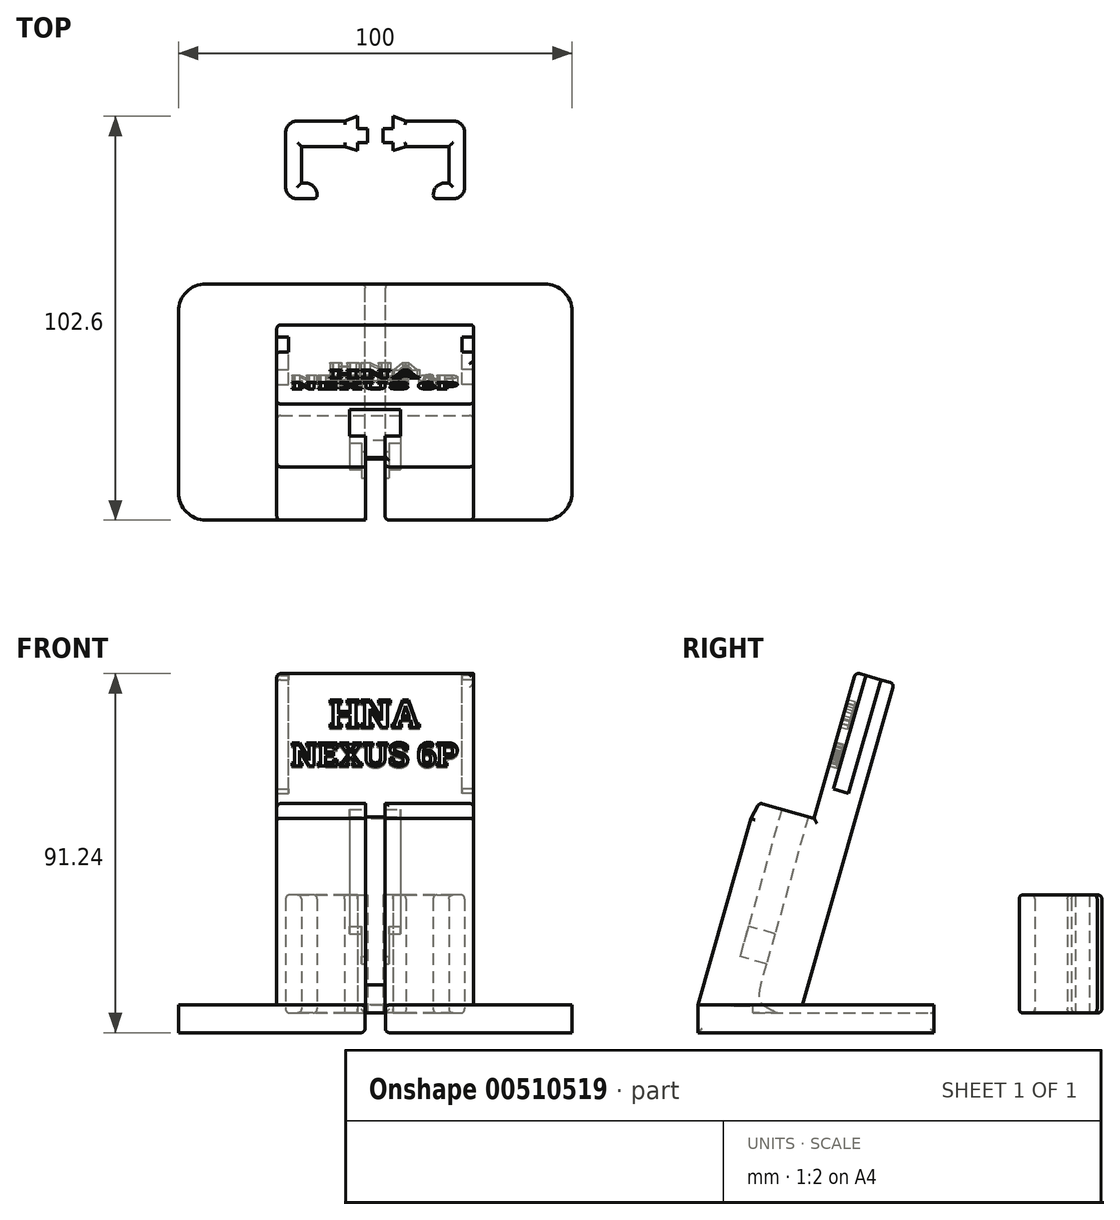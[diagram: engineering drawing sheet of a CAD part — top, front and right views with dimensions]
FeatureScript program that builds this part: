
annotation { "Feature Type Name" : "Feature", "Feature Type Description" : "" }
export const myFeature = defineFeature(function(context is Context, id is Id, definition is map)
    precondition{}
    {
        {
            var Q0;
            Q0=qCreatedBy(makeId("Top.planeOp"),FACE);
            var sketch = newSketch(context, id + "F0", { "sketchPlane" : qUnion([Q0])});
            skLineSegment(sketch, "E0.bottom", {"start": v(50, -30) * mm, "end": v(-50, -30) * mm});
            skLineSegment(sketch, "E0.top", {"start": v(50, 30) * mm, "end": v(-50, 30) * mm});
            skLineSegment(sketch, "E0.left", {"start": v(50, -30) * mm, "end": v(50, 30) * mm});
            skLineSegment(sketch, "E0.right", {"start": v(-50, -30) * mm, "end": v(-50, 30) * mm});
            skPoint(sketch, "E0.middle", {"position": v(0, 0) * mm});
            skLineSegment(sketch, "E1.top", {"start": v(25, -4) * mm, "end": v(-25, -4) * mm});
            skLineSegment(sketch, "E1.left", {"start": v(25, -30) * mm, "end": v(25, -4) * mm});
            skLineSegment(sketch, "E1.right", {"start": v(-25, -30) * mm, "end": v(-25, -4) * mm});
            skPoint(sketch, "E1.middle", {"position": v(0, -17) * mm});
            skLineSegment(sketch, "E2", {"start": v(0, -28.9) * mm, "end": v(-2.6, -28.9) * mm, "construction": true});
            skLineSegment(sketch, "E3", {"start": v(-2.6, -30) * mm, "end": v(-2.6, 30) * mm});
            skLineSegment(sketch, "E4", {"start": v(0, -28.9) * mm, "end": v(2.6, -28.9) * mm});
            skLineSegment(sketch, "E5", {"start": v(2.6, -30) * mm, "end": v(2.6, 30) * mm});
            skLineSegment(sketch, "E6", {"start": v(2.6, -16) * mm, "end": v(-2.6, -16) * mm});
            skLineSegment(sketch, "E7", {"start": v(-2.5, 71.41) * mm, "end": v(-20.75, 71.41) * mm});
            skLineSegment(sketch, "E8", {"start": v(-20.75, 71.41) * mm, "end": v(-20.75, 51.61) * mm});
            skLineSegment(sketch, "E9", {"start": v(-20.75, 51.61) * mm, "end": v(-12.75, 51.61) * mm});
            skLineSegment(sketch, "E10", {"start": v(-12.75, 51.61) * mm, "end": v(-12.75, 55.61) * mm});
            skLineSegment(sketch, "E11", {"start": v(-12.75, 55.61) * mm, "end": v(-16.75, 55.61) * mm});
            skLineSegment(sketch, "E12", {"start": v(-16.75, 55.61) * mm, "end": v(-16.75, 64.91) * mm});
            skLineSegment(sketch, "E13", {"start": v(-16.75, 64.91) * mm, "end": v(-2.5, 64.91) * mm});
            skLineSegment(sketch, "E14", {"start": v(0, 65.91) * mm, "end": v(0, 69.41) * mm});
            skLineSegment(sketch, "E15", {"start": v(-2.5, 64.91) * mm, "end": v(-2.5, 65.91) * mm});
            skLineSegment(sketch, "E16", {"start": v(-2.5, 65.91) * mm, "end": v(0, 65.91) * mm});
            skLineSegment(sketch, "E17", {"start": v(-2.5, 71.41) * mm, "end": v(-2.5, 69.41) * mm});
            skLineSegment(sketch, "E18", {"start": v(-2.5, 69.41) * mm, "end": v(0, 69.41) * mm});
            skLineSegment(sketch, "E19", {"start": v(-5.78, 71.41) * mm, "end": v(-2.5, 72.6) * mm});
            skLineSegment(sketch, "E20", {"start": v(-2.5, 72.6) * mm, "end": v(-2.5, 71.41) * mm});
            skLineSegment(sketch, "E21", {"start": v(-2.5, 64.91) * mm, "end": v(-2.5, 63.9) * mm});
            skLineSegment(sketch, "E22", {"start": v(-2.5, 63.9) * mm, "end": v(-5.78, 64.91) * mm});
            skSolve(sketch);
        }
        {
            var Q0;
            {var subQ4=sQuery(id+"F0.wireOp",EDGE,"E0.right");Q0=makeQuery(id+"F0.imprint","IMPRINT",FACE,{"disambiguationData":[TD([[makeQuery(id+"F0.imprint","IMPRINT",EDGE,{"derivedFrom":subQ4}),-1.0]])]});}
            var Q1;
            {var subQ0=sQuery(id+"F0.wireOp",EDGE,"E1.right");Q1=makeQuery(id+"F0.imprint","IMPRINT",FACE,{"disambiguationData":[TD([[makeQuery(id+"F0.imprint","IMPRINT",EDGE,{"derivedFrom":subQ0}),-1.0]])]});}
            var Q2;
            {var subQ4=sQuery(id+"F0.wireOp",EDGE,"E1.left");Q2=makeQuery(id+"F0.imprint","IMPRINT",FACE,{"disambiguationData":[TD([[makeQuery(id+"F0.imprint","IMPRINT",EDGE,{"derivedFrom":subQ4}),1.0]])]});}
            var Q3;
            {var subQ0=sQuery(id+"F0.wireOp",EDGE,"E0.left");Q3=makeQuery(id+"F0.imprint","IMPRINT",FACE,{"disambiguationData":[TD([[makeQuery(id+"F0.imprint","IMPRINT",EDGE,{"derivedFrom":subQ0}),1.0]])]});}
            extrude(context, id + "F1", {"entities" : qUnion([Q0, Q1, Q2, Q3]), "oppositeDirection" : true, "depth" : 5 * mm});
        }
        {
            var Q0;
            {var subQ4=sQuery(id+"F0.wireOp",EDGE,"E0.right");Q0=makeQuery(id+"F0.imprint","IMPRINT",FACE,{"disambiguationData":[TD([[makeQuery(id+"F0.imprint","IMPRINT",EDGE,{"derivedFrom":subQ4}),-1.0]])]});}
            var Q1;
            {var subQ0=sQuery(id+"F0.wireOp",EDGE,"E1.right");Q1=makeQuery(id+"F0.imprint","IMPRINT",FACE,{"disambiguationData":[TD([[makeQuery(id+"F0.imprint","IMPRINT",EDGE,{"derivedFrom":subQ0}),-1.0]])]});}
            var Q2;
            {var subQ0=sQuery(id+"F0.wireOp",EDGE,"E3");var subQ1=sQuery(id+"F0.wireOp",EDGE,"E0.top");var subQ2=makeQuery(id+"F0.imprint","INTERSECT",VERTEX,{"derivedFrom":[subQ1,subQ0]});Q2=makeQuery(id+"F0.imprint","IMPRINT",FACE,{"disambiguationData":[TD([[makeQuery(id+"F0.imprint","IMPRINT",EDGE,{"disambiguationData":[TD([[subQ2,1.0]])],"derivedFrom":subQ1}),1.0]])]});}
            var Q3;
            {var subQ4=sQuery(id+"F0.wireOp",EDGE,"E1.left");Q3=makeQuery(id+"F0.imprint","IMPRINT",FACE,{"disambiguationData":[TD([[makeQuery(id+"F0.imprint","IMPRINT",EDGE,{"derivedFrom":subQ4}),1.0]])]});}
            var Q4;
            {var subQ0=sQuery(id+"F0.wireOp",EDGE,"E0.left");Q4=makeQuery(id+"F0.imprint","IMPRINT",FACE,{"disambiguationData":[TD([[makeQuery(id+"F0.imprint","IMPRINT",EDGE,{"derivedFrom":subQ0}),1.0]])]});}
            var Q5;
            {var subQ5=sQuery(id+"F0.wireOp",EDGE,"E6");Q5=makeQuery(id+"F0.imprint","IMPRINT",FACE,{"disambiguationData":[TD([[makeQuery(id+"F0.imprint","IMPRINT",EDGE,{"derivedFrom":subQ5}),-1.0]])]});}
            extrude(context, id + "F2", {"entities" : qUnion([Q0, Q1, Q2, Q3, Q4, Q5]), "operationType" : NewBodyOperationType.ADD, "depth" : 2 * mm});
        }
        {
            var Q0;
            Q0=makeQuery(id+"F2.opExtrude","CAP_FACE",FACE,{"disambiguationData":[OSD([sQuery(id+"F0.wireOp",EDGE,"E0.bottom"),sQuery(id+"F0.wireOp",EDGE,"E0.top"),sQuery(id+"F0.wireOp",EDGE,"E0.left"),sQuery(id+"F0.wireOp",EDGE,"E0.right"),sQuery(id+"F0.wireOp",EDGE,"E1.top"),sQuery(id+"F0.wireOp",EDGE,"E3"),sQuery(id+"F0.wireOp",EDGE,"E5")])],"isStart":false});
            var sketch = newSketch(context, id + "F3", { "sketchPlane" : qUnion([Q0])});
            skLineSegment(sketch, "E23.bottom", {"start": v(50, -30) * mm, "end": v(-50, -30) * mm});
            skLineSegment(sketch, "E23.top", {"start": v(50, 30) * mm, "end": v(-50, 30) * mm});
            skLineSegment(sketch, "E23.left", {"start": v(50, -30) * mm, "end": v(50, 30) * mm});
            skLineSegment(sketch, "E23.right", {"start": v(-50, -30) * mm, "end": v(-50, 30) * mm});
            skPoint(sketch, "E23.middle", {"position": v(0, 0) * mm});
            skLineSegment(sketch, "E24.top", {"start": v(25, -4) * mm, "end": v(-25, -4) * mm});
            skLineSegment(sketch, "E24.left", {"start": v(25, -30) * mm, "end": v(25, -4) * mm});
            skLineSegment(sketch, "E24.right", {"start": v(-25, -30) * mm, "end": v(-25, -4) * mm});
            skPoint(sketch, "E24.middle", {"position": v(0, -17) * mm});
            skLineSegment(sketch, "E25", {"start": v(0, -20.22) * mm, "end": v(-2.6, -20.22) * mm, "construction": true});
            skLineSegment(sketch, "E26", {"start": v(0, -20.22) * mm, "end": v(2.6, -20.22) * mm});
            skLineSegment(sketch, "E27", {"start": v(-2.6, -16) * mm, "end": v(2.6, -16) * mm});
            skSolve(sketch);
        }
        {
            var Q0;
            Q0=qCreatedBy(makeId("Right.planeOp"),FACE);
            var sketch = newSketch(context, id + "F4", { "sketchPlane" : qUnion([Q0])});
            skLineSegment(sketch, "E28", {"start": v(-30, 2) * mm, "end": v(-16.48, 49.44) * mm});
            skLineSegment(sketch, "E29", {"start": v(-16.48, 49.44) * mm, "end": v(10.06, 49.44) * mm});
            skLineSegment(sketch, "E30", {"start": v(10.06, 49.44) * mm, "end": v(-3.6, 1.55) * mm});
            skLineSegment(sketch, "E31", {"start": v(-3.6, 1.55) * mm, "end": v(-30, 2) * mm});
            skLineSegment(sketch, "E32", {"start": v(10.06, 49.44) * mm, "end": v(20.62, 86.48) * mm});
            skLineSegment(sketch, "E33", {"start": v(20.62, 86.48) * mm, "end": v(10.06, 86.48) * mm});
            skLineSegment(sketch, "E34", {"start": v(10.06, 86.48) * mm, "end": v(-0.5, 49.44) * mm});
            skLineSegment(sketch, "E35", {"start": v(-0.5, 49.44) * mm, "end": v(-1.94, 49.85) * mm});
            skLineSegment(sketch, "E36", {"start": v(-1.94, 49.85) * mm, "end": v(-10.41, 20.13) * mm});
            skLineSegment(sketch, "E37.0", {"start": v(-8.67, 51.77) * mm, "end": v(-17.14, 22.05) * mm});
            skLineSegment(sketch, "E38", {"start": v(-10.41, 20.13) * mm, "end": v(-17.14, 22.05) * mm});
            skLineSegment(sketch, "E39", {"start": v(-8.67, 51.77) * mm, "end": v(-14.37, 53.39) * mm});
            skLineSegment(sketch, "E40", {"start": v(-14.37, 53.39) * mm, "end": v(-16.48, 49.44) * mm});
            skLineSegment(sketch, "E41", {"start": v(-10.41, 20.13) * mm, "end": v(-12.6, 12.44) * mm});
            skLineSegment(sketch, "E42.0", {"start": v(-17.14, 22.05) * mm, "end": v(-19.34, 14.36) * mm});
            skLineSegment(sketch, "E43", {"start": v(-12.6, 12.44) * mm, "end": v(-19.34, 14.36) * mm});
            skLineSegment(sketch, "E44", {"start": v(-12.6, 12.44) * mm, "end": v(-15.65, 1.75) * mm});
            skLineSegment(sketch, "E45", {"start": v(-19.34, 14.36) * mm, "end": v(-22.9, 1.88) * mm});
            skPoint(sketch, "E46.1.internal.snap0", {"position": v(-14.13, 7.1) * mm});
            skFitSpline(sketch, "E46", {"points": [v(-14.13, 7.1) * mm, v(-14.13, 2.85) * mm, v(-9.8, 0) * mm], "startDerivative": vector(-1.86, -9.65) * mm, "endDerivative": vector(10, -5.58) * mm});
            skLineSegment(sketch, "E47", {"start": v(-9.8, 0) * mm, "end": v(-30.07, 0) * mm});
            skLineSegment(sketch, "E48", {"start": v(-30.07, 0) * mm, "end": v(-30, 2) * mm});
            skLineSegment(sketch, "E49", {"start": v(-1.94, 49.85) * mm, "end": v(-8.67, 51.77) * mm});
            skLineSegment(sketch, "E50", {"start": v(10.06, 86.48) * mm, "end": v(19.83, 83.7) * mm});
            skSolve(sketch);
        }
        {
            var Q0;
            {var subQ3=sQuery(id+"F4.wireOp",EDGE,"E28");Q0=makeQuery(id+"F4.imprint","IMPRINT",FACE,{"disambiguationData":[TD([[makeQuery(id+"F4.imprint","IMPRINT",EDGE,{"derivedFrom":subQ3}),-1.0]])]});}
            var Q1;
            Q1=makeQuery(id+"F4.imprint","IMPRINT",FACE,{"disambiguationData":[TD([[makeQuery(id+"F4.imprint","IMPRINT",EDGE,{"derivedFrom":sQuery(id+"F4.wireOp",EDGE,"E43")}),1.0]])]});
            var Q2;
            {var subQ4=sQuery(id+"F4.wireOp",EDGE,"E41");Q2=makeQuery(id+"F4.imprint","IMPRINT",FACE,{"disambiguationData":[TD([[makeQuery(id+"F4.imprint","IMPRINT",EDGE,{"derivedFrom":subQ4}),-1.0]])]});}
            var Q3;
            {var subQ1=sQuery(id+"F4.wireOp",EDGE,"E30");Q3=makeQuery(id+"F4.imprint","IMPRINT",FACE,{"disambiguationData":[TD([[makeQuery(id+"F4.imprint","IMPRINT",EDGE,{"derivedFrom":subQ1}),-1.0]])]});}
            var Q4;
            {var subQ4=sQuery(id+"F4.wireOp",EDGE,"E39");Q4=makeQuery(id+"F4.imprint","IMPRINT",FACE,{"disambiguationData":[TD([[makeQuery(id+"F4.imprint","IMPRINT",EDGE,{"derivedFrom":subQ4}),1.0]])]});}
            var Q5;
            {var subQ0=sQuery(id+"F4.wireOp",EDGE,"E35");Q5=makeQuery(id+"F4.imprint","IMPRINT",FACE,{"disambiguationData":[TD([[makeQuery(id+"F4.imprint","IMPRINT",EDGE,{"derivedFrom":subQ0}),1.0]])]});}
            var Q6;
            {var subQ0=sQuery(id+"F4.wireOp",EDGE,"E44");var subQ1=sQuery(id+"F4.wireOp",EDGE,"E31");var subQ2=makeQuery(id+"F4.imprint","INTERSECT",VERTEX,{"derivedFrom":[subQ1,subQ0]});Q6=makeQuery(id+"F4.imprint","IMPRINT",FACE,{"disambiguationData":[TD([[makeQuery(id+"F4.imprint","IMPRINT",EDGE,{"disambiguationData":[TD([[subQ2,1.0]])],"derivedFrom":subQ1}),-1.0]])]});}
            var Q7;
            {var subQ5=sQuery(id+"F4.wireOp",EDGE,"E49");Q7=makeQuery(id+"F4.imprint","IMPRINT",FACE,{"disambiguationData":[TD([[makeQuery(id+"F4.imprint","IMPRINT",EDGE,{"derivedFrom":subQ5}),1.0]])]});}
            var Q8;
            {var subQ3=sQuery(id+"F4.wireOp",EDGE,"E34");Q8=makeQuery(id+"F4.imprint","IMPRINT",FACE,{"disambiguationData":[TD([[makeQuery(id+"F4.imprint","IMPRINT",EDGE,{"derivedFrom":subQ3}),1.0]])]});}
            var Q9;
            {var subQ5=sQuery(id+"F4.wireOp",EDGE,"E38");Q9=makeQuery(id+"F4.imprint","IMPRINT",FACE,{"disambiguationData":[TD([[makeQuery(id+"F4.imprint","IMPRINT",EDGE,{"derivedFrom":subQ5}),-1.0]])]});}
            extrude(context, id + "F5", {"entities" : qUnion([Q0, Q1, Q2, Q3, Q4, Q5, Q6, Q7, Q8, Q9]), "operationType" : NewBodyOperationType.ADD, "endBound" : BoundingType.SYMMETRIC, "oppositeDirection" : true, "depth" : 50 * mm});
        }
        {
            var Q0;
            {var subQ5=sQuery(id+"F4.wireOp",EDGE,"E49");Q0=makeQuery(id+"F4.imprint","IMPRINT",FACE,{"disambiguationData":[TD([[makeQuery(id+"F4.imprint","IMPRINT",EDGE,{"derivedFrom":subQ5}),1.0]])]});}
            var Q1;
            {var subQ5=sQuery(id+"F4.wireOp",EDGE,"E38");Q1=makeQuery(id+"F4.imprint","IMPRINT",FACE,{"disambiguationData":[TD([[makeQuery(id+"F4.imprint","IMPRINT",EDGE,{"derivedFrom":subQ5}),-1.0]])]});}
            extrude(context, id + "F6", {"entities" : qUnion([Q0, Q1]), "operationType" : NewBodyOperationType.REMOVE, "endBound" : BoundingType.SYMMETRIC, "oppositeDirection" : true, "depth" : 13 * mm});
        }
        {
            var Q0;
            {var subQ4=sQuery(id+"F4.wireOp",EDGE,"E47");Q0=makeQuery(id+"F4.imprint","IMPRINT",FACE,{"disambiguationData":[TD([[makeQuery(id+"F4.imprint","IMPRINT",EDGE,{"derivedFrom":subQ4}),-1.0]])]});}
            var Q1;
            {var subQ0=sQuery(id+"F4.wireOp",EDGE,"E44");var subQ1=sQuery(id+"F4.wireOp",EDGE,"E31");var subQ2=makeQuery(id+"F4.imprint","INTERSECT",VERTEX,{"derivedFrom":[subQ1,subQ0]});Q1=makeQuery(id+"F4.imprint","IMPRINT",FACE,{"disambiguationData":[TD([[makeQuery(id+"F4.imprint","IMPRINT",EDGE,{"disambiguationData":[TD([[subQ2,1.0]])],"derivedFrom":subQ1}),-1.0]])]});}
            var Q2;
            {var subQ4=sQuery(id+"F4.wireOp",EDGE,"E43");Q2=makeQuery(id+"F4.imprint","IMPRINT",FACE,{"disambiguationData":[TD([[makeQuery(id+"F4.imprint","IMPRINT",EDGE,{"derivedFrom":subQ4}),1.0]])]});}
            var Q3;
            {var subQ5=sQuery(id+"F4.wireOp",EDGE,"E28");Q3=makeQuery(id+"F4.imprint","IMPRINT",FACE,{"disambiguationData":[TD([[makeQuery(id+"F4.imprint","IMPRINT",EDGE,{"derivedFrom":subQ5}),-1.0]])]});}
            var Q4;
            {var subQ4=sQuery(id+"F4.wireOp",EDGE,"E39");Q4=makeQuery(id+"F4.imprint","IMPRINT",FACE,{"disambiguationData":[TD([[makeQuery(id+"F4.imprint","IMPRINT",EDGE,{"derivedFrom":subQ4}),1.0]])]});}
            extrude(context, id + "F7", {"entities" : qUnion([Q0, Q1, Q2, Q3, Q4]), "operationType" : NewBodyOperationType.REMOVE, "endBound" : BoundingType.SYMMETRIC, "depth" : 5 * mm});
        }
        {
            var Q0;
            Q0=makeQuery(id+"F4.imprint","IMPRINT",FACE,{"disambiguationData":[TD([[makeQuery(id+"F4.imprint","IMPRINT",EDGE,{"derivedFrom":sQuery(id+"F4.wireOp",EDGE,"E38")}),1.0]])]});
            extrude(context, id + "F8", {"entities" : qUnion([Q0]), "operationType" : NewBodyOperationType.REMOVE, "endBound" : BoundingType.SYMMETRIC, "oppositeDirection" : true, "depth" : 7 * mm});
        }
        {
            var Q0;
            Q0=makeQuery(id+"F5.opExtrude","SWEPT_FACE",FACE,{"disambiguationData":[OSD([sQuery(id+"F4.wireOp",EDGE,"E50")])]});
            var sketch = newSketch(context, id + "F9", { "sketchPlane" : qUnion([Q0])});
            skLineSegment(sketch, "E51.bottom", {"start": v(-25, -11.33) * mm, "end": v(-22, -11.33) * mm});
            skLineSegment(sketch, "E51.top", {"start": v(-25, -7.33) * mm, "end": v(-22, -7.33) * mm});
            skLineSegment(sketch, "E51.left", {"start": v(-25, -11.33) * mm, "end": v(-25, -7.33) * mm});
            skLineSegment(sketch, "E51.right", {"start": v(-22, -11.33) * mm, "end": v(-22, -7.33) * mm});
            skLineSegment(sketch, "E52.MirrorCS", {"start": v(22, -11.33) * mm, "end": v(22, -7.33) * mm});
            skLineSegment(sketch, "E53.MirrorCS", {"start": v(25, -7.33) * mm, "end": v(22, -7.33) * mm});
            skLineSegment(sketch, "E54.MirrorCS", {"start": v(25, -11.33) * mm, "end": v(22, -11.33) * mm});
            skLineSegment(sketch, "E55.MirrorCS", {"start": v(25, -11.33) * mm, "end": v(25, -7.33) * mm});
            skSolve(sketch);
        }
        {
            var Q0;
            Q0=makeQuery(id+"F9.imprint","IMPRINT",FACE,{"disambiguationData":[TD([[makeQuery(id+"F9.imprint","IMPRINT",EDGE,{"derivedFrom":sQuery(id+"F9.wireOp",EDGE,"E52.MirrorCS")}),-1.0]])]});
            var Q1;
            Q1=makeQuery(id+"F9.imprint","IMPRINT",FACE,{"disambiguationData":[TD([[makeQuery(id+"F9.imprint","IMPRINT",EDGE,{"derivedFrom":sQuery(id+"F9.wireOp",EDGE,"E51.bottom")}),1.0]])]});
            extrude(context, id + "F10", {"entities" : qUnion([Q0, Q1]), "operationType" : NewBodyOperationType.REMOVE, "oppositeDirection" : true, "depth" : 30 * mm});
        }
        {
            var Q0;
            Q0=makeQuery(id+"F5.opExtrude","SWEPT_FACE",FACE,{"disambiguationData":[OSD([sQuery(id+"F4.wireOp",EDGE,"E34")])]});
            var sketch = newSketch(context, id + "F11", { "sketchPlane" : qUnion([Q0])});
            skText(sketch, "E56", { "text": "HNA", "fontName": "RobotoSlab-Bold.ttf"});
            skText(sketch, "E57", { "text": "NEXUS 6P", "fontName": "RobotoSlab-Bold.ttf"});
            const initialGuessF11  = {"E56": [-0.0118, 0.07148, 1, 0, 0.00735], "E57": [-0.02139, 0.06127, 1, 0, 0.0062]};
            skSetInitialGuess(sketch, initialGuessF11);
            skSolve(sketch);
        }
        {
            var Q0;
            Q0=makeQuery(id+"F11.imprint","IMPRINT",FACE,{"disambiguationData":[TD([[makeQuery(id+"F11.imprint","IMPRINT",EDGE,{"derivedFrom":sQuery(id+"F11.wireOp",EDGE,"E56.sketch_text.stroke-54")}),-1.0]])]});
            var Q1;
            Q1=makeQuery(id+"F11.imprint","IMPRINT",FACE,{"disambiguationData":[TD([[makeQuery(id+"F11.imprint","IMPRINT",EDGE,{"derivedFrom":sQuery(id+"F11.wireOp",EDGE,"E56.sketch_text.stroke-30")}),-1.0]])]});
            var Q2;
            Q2=makeQuery(id+"F11.imprint","IMPRINT",FACE,{"disambiguationData":[TD([[makeQuery(id+"F11.imprint","IMPRINT",EDGE,{"derivedFrom":sQuery(id+"F11.wireOp",EDGE,"E56.sketch_text.stroke-0")}),-1.0]])]});
            var Q3;
            Q3=makeQuery(id+"F11.imprint","IMPRINT",FACE,{"disambiguationData":[TD([[makeQuery(id+"F11.imprint","IMPRINT",EDGE,{"derivedFrom":sQuery(id+"F11.wireOp",EDGE,"E57.sketch_text.stroke-155")}),-1.0]])]});
            var Q4;
            Q4=makeQuery(id+"F11.imprint","IMPRINT",FACE,{"disambiguationData":[TD([[makeQuery(id+"F11.imprint","IMPRINT",EDGE,{"derivedFrom":sQuery(id+"F11.wireOp",EDGE,"E57.sketch_text.stroke-127")}),-1.0]])]});
            var Q5;
            Q5=makeQuery(id+"F11.imprint","IMPRINT",FACE,{"disambiguationData":[TD([[makeQuery(id+"F11.imprint","IMPRINT",EDGE,{"derivedFrom":sQuery(id+"F11.wireOp",EDGE,"E57.sketch_text.stroke-97")}),-1.0]])]});
            var Q6;
            Q6=makeQuery(id+"F11.imprint","IMPRINT",FACE,{"disambiguationData":[TD([[makeQuery(id+"F11.imprint","IMPRINT",EDGE,{"derivedFrom":sQuery(id+"F11.wireOp",EDGE,"E57.sketch_text.stroke-73")}),-1.0]])]});
            var Q7;
            Q7=makeQuery(id+"F11.imprint","IMPRINT",FACE,{"disambiguationData":[TD([[makeQuery(id+"F11.imprint","IMPRINT",EDGE,{"derivedFrom":sQuery(id+"F11.wireOp",EDGE,"E57.sketch_text.stroke-45")}),-1.0]])]});
            var Q8;
            Q8=makeQuery(id+"F11.imprint","IMPRINT",FACE,{"disambiguationData":[TD([[makeQuery(id+"F11.imprint","IMPRINT",EDGE,{"derivedFrom":sQuery(id+"F11.wireOp",EDGE,"E57.sketch_text.stroke-24")}),-1.0]])]});
            var Q9;
            Q9=makeQuery(id+"F11.imprint","IMPRINT",FACE,{"disambiguationData":[TD([[makeQuery(id+"F11.imprint","IMPRINT",EDGE,{"derivedFrom":sQuery(id+"F11.wireOp",EDGE,"E57.sketch_text.stroke-0")}),-1.0]])]});
            extrude(context, id + "F12", {"entities" : qUnion([Q0, Q1, Q2, Q3, Q4, Q5, Q6, Q7, Q8, Q9]), "operationType" : NewBodyOperationType.REMOVE, "oppositeDirection" : true, "depth" : 2 * mm});
        }
        {
            var Q0;
            {var subQ0=sQuery(id+"F4.wireOp",EDGE,"E50");var subQ1=sQuery(id+"F4.wireOp",EDGE,"E34");Q0=makeQuery(id+"F10.boolean.opBoolean","SPLIT",EDGE,{"disambiguationData":[TD([makeQuery(id+"F5.opExtrude","SWEPT_FACE",FACE,{"disambiguationData":[OSD([subQ1])]})])],"derivedFrom":makeQuery(id+"F5.opExtrude","CAP_EDGE",EDGE,{"disambiguationData":[OSD([subQ0])],"isStart":false})});}
            var Q1;
            {var subQ0=sQuery(id+"F4.wireOp",EDGE,"E50");Q1=makeQuery(id+"F10.boolean.opBoolean","SPLIT",EDGE,{"disambiguationData":[TD([makeQuery(id+"F10.opExtrude","SWEPT_FACE",FACE,{"disambiguationData":[OSD([sQuery(id+"F9.wireOp",EDGE,"E51.top")])]})])],"derivedFrom":makeQuery(id+"F5.opExtrude","CAP_EDGE",EDGE,{"disambiguationData":[OSD([subQ0])],"isStart":false})});}
            var Q2;
            Q2=makeQuery(id+"F10.boolean.opBoolean","COPY",EDGE,{"derivedFrom":makeQuery(id+"F10.opExtrude","SWEPT_EDGE",EDGE,{"disambiguationData":[OSD([sQuery(id+"F4.wireOp",EDGE,"E50"),sQuery(id+"F9.wireOp",EDGE,"E51.top"),sQuery(id+"F9.wireOp",EDGE,"E51.left")])]})});
            var Q3;
            Q3=makeQuery(id+"F10.boolean.opBoolean","COPY",EDGE,{"derivedFrom":makeQuery(id+"F10.opExtrude","SWEPT_EDGE",EDGE,{"disambiguationData":[OSD([sQuery(id+"F4.wireOp",EDGE,"E50"),sQuery(id+"F9.wireOp",EDGE,"E51.bottom"),sQuery(id+"F9.wireOp",EDGE,"E51.left")])]})});
            var Q4;
            Q4=makeQuery(id+"F10.boolean.opBoolean","COPY",EDGE,{"derivedFrom":makeQuery(id+"F10.opExtrude","CAP_EDGE",EDGE,{"disambiguationData":[OSD([sQuery(id+"F9.wireOp",EDGE,"E51.left")])],"isStart":false})});
            var Q5;
            Q5=makeQuery(id+"F10.boolean.opBoolean","COPY",EDGE,{"derivedFrom":makeQuery(id+"F10.opExtrude","CAP_EDGE",EDGE,{"disambiguationData":[OSD([sQuery(id+"F9.wireOp",EDGE,"E51.top")])],"isStart":true})});
            var Q6;
            Q6=makeQuery(id+"F5.opExtrude","CAP_EDGE",EDGE,{"disambiguationData":[OSD([sQuery(id+"F4.wireOp",EDGE,"E34")])],"isStart":false});
            var Q7;
            Q7=makeQuery(id+"F5.opExtrude","CAP_EDGE",EDGE,{"disambiguationData":[OSD([sQuery(id+"F4.wireOp",EDGE,"E30"),sQuery(id+"F4.wireOp",EDGE,"E32")])],"isStart":false});
            var Q8;
            Q8=makeQuery(id+"F10.boolean.opBoolean","COPY",EDGE,{"derivedFrom":makeQuery(id+"F10.opExtrude","CAP_EDGE",EDGE,{"disambiguationData":[OSD([sQuery(id+"F9.wireOp",EDGE,"E51.right")])],"isStart":true})});
            var Q9;
            Q9=makeQuery(id+"F5.opExtrude","SWEPT_EDGE",EDGE,{"disambiguationData":[OSD([sQuery(id+"F4.wireOp",EDGE,"E33"),sQuery(id+"F4.wireOp",EDGE,"E34"),sQuery(id+"F4.wireOp",EDGE,"E50")])]});
            var Q10;
            Q10=makeQuery(id+"F5.opExtrude","SWEPT_EDGE",EDGE,{"disambiguationData":[OSD([sQuery(id+"F4.wireOp",EDGE,"E32"),sQuery(id+"F4.wireOp",EDGE,"E50")])]});
            var Q11;
            {var subQ0=sQuery(id+"F4.wireOp",EDGE,"E49");var subQ1=sQuery(id+"F4.wireOp",EDGE,"E40");var subQ2=sQuery(id+"F4.wireOp",EDGE,"E39");var subQ3=sQuery(id+"F4.wireOp",EDGE,"E35");var subQ4=sQuery(id+"F4.wireOp",EDGE,"E28");Q11=makeQuery(id+"F7.boolean.opBoolean","SPLIT",EDGE,{"disambiguationData":[TD([makeQuery(id+"F5.opExtrude","CAP_FACE",FACE,{"disambiguationData":[OSD([subQ4,sQuery(id+"F4.wireOp",EDGE,"E30"),sQuery(id+"F4.wireOp",EDGE,"E31"),sQuery(id+"F4.wireOp",EDGE,"E32"),sQuery(id+"F4.wireOp",EDGE,"E34"),subQ3,subQ2,subQ1,subQ0,sQuery(id+"F4.wireOp",EDGE,"E50")])],"isStart":false})])],"derivedFrom":makeQuery(id+"F5.opExtrude","SWEPT_EDGE",EDGE,{"disambiguationData":[OSD([subQ2,subQ1])]})});}
            var Q12;
            Q12=makeQuery(id+"F5.opExtrude","CAP_EDGE",EDGE,{"disambiguationData":[OSD([sQuery(id+"F4.wireOp",EDGE,"E35"),sQuery(id+"F4.wireOp",EDGE,"E39"),sQuery(id+"F4.wireOp",EDGE,"E49")])],"isStart":false});
            var Q13;
            {var subQ0=sQuery(id+"F4.wireOp",EDGE,"E49");var subQ1=sQuery(id+"F4.wireOp",EDGE,"E40");var subQ2=sQuery(id+"F4.wireOp",EDGE,"E39");var subQ3=sQuery(id+"F4.wireOp",EDGE,"E35");var subQ4=sQuery(id+"F4.wireOp",EDGE,"E28");Q13=makeQuery(id+"F7.boolean.opBoolean","SPLIT",EDGE,{"disambiguationData":[TD([makeQuery(id+"F5.opExtrude","CAP_FACE",FACE,{"disambiguationData":[OSD([subQ4,sQuery(id+"F4.wireOp",EDGE,"E30"),sQuery(id+"F4.wireOp",EDGE,"E31"),sQuery(id+"F4.wireOp",EDGE,"E32"),sQuery(id+"F4.wireOp",EDGE,"E34"),subQ3,subQ2,subQ1,subQ0,sQuery(id+"F4.wireOp",EDGE,"E50")])],"isStart":true})])],"derivedFrom":makeQuery(id+"F5.opExtrude","SWEPT_EDGE",EDGE,{"disambiguationData":[OSD([subQ2,subQ1])]})});}
            var Q14;
            Q14=makeQuery(id+"F5.opExtrude","CAP_EDGE",EDGE,{"disambiguationData":[OSD([sQuery(id+"F4.wireOp",EDGE,"E35"),sQuery(id+"F4.wireOp",EDGE,"E39"),sQuery(id+"F4.wireOp",EDGE,"E49")])],"isStart":true});
            var Q15;
            Q15=makeQuery(id+"F7.boolean.opBoolean","COPY",EDGE,{"derivedFrom":makeQuery(id+"F7.opExtrude","CAP_EDGE",EDGE,{"disambiguationData":[OSD([sQuery(id+"F4.wireOp",EDGE,"E39")])],"isStart":false})});
            var Q16;
            Q16=makeQuery(id+"F7.boolean.opBoolean","COPY",EDGE,{"derivedFrom":makeQuery(id+"F7.opExtrude","CAP_EDGE",EDGE,{"disambiguationData":[OSD([sQuery(id+"F4.wireOp",EDGE,"E39")])],"isStart":true})});
            var Q17;
            Q17=makeQuery(id+"F6.boolean.opBoolean","COPY",EDGE,{"derivedFrom":makeQuery(id+"F6.opExtrude","CAP_EDGE",EDGE,{"disambiguationData":[OSD([sQuery(id+"F4.wireOp",EDGE,"E49")])],"isStart":true})});
            var Q18;
            Q18=makeQuery(id+"F6.boolean.opBoolean","COPY",EDGE,{"derivedFrom":makeQuery(id+"F6.opExtrude","SWEPT_EDGE",EDGE,{"disambiguationData":[OSD([sQuery(id+"F4.wireOp",EDGE,"E35"),sQuery(id+"F4.wireOp",EDGE,"E36"),sQuery(id+"F4.wireOp",EDGE,"E49")])]})});
            var Q19;
            Q19=makeQuery(id+"F6.boolean.opBoolean","COPY",EDGE,{"derivedFrom":makeQuery(id+"F6.opExtrude","CAP_EDGE",EDGE,{"disambiguationData":[OSD([sQuery(id+"F4.wireOp",EDGE,"E49")])],"isStart":false})});
            var Q20;
            {var subQ0=sQuery(id+"F4.wireOp",EDGE,"E49");var subQ1=sQuery(id+"F4.wireOp",EDGE,"E39");var subQ2=sQuery(id+"F4.wireOp",EDGE,"E37.0");Q20=makeQuery(id+"F7.boolean.opBoolean","SPLIT",EDGE,{"disambiguationData":[TD([makeQuery(id+"F6.boolean.opBoolean","COPY",FACE,{"derivedFrom":makeQuery(id+"F6.opExtrude","CAP_FACE",FACE,{"disambiguationData":[OSD([sQuery(id+"F4.wireOp",EDGE,"E36"),subQ2,sQuery(id+"F4.wireOp",EDGE,"E38"),subQ0])],"isStart":false})})])],"derivedFrom":makeQuery(id+"F6.boolean.opBoolean","COPY",EDGE,{"derivedFrom":makeQuery(id+"F6.opExtrude","SWEPT_EDGE",EDGE,{"disambiguationData":[OSD([subQ2,subQ1,subQ0])]})})});}
            var Q21;
            {var subQ0=sQuery(id+"F4.wireOp",EDGE,"E49");var subQ1=sQuery(id+"F4.wireOp",EDGE,"E39");var subQ2=sQuery(id+"F4.wireOp",EDGE,"E37.0");Q21=makeQuery(id+"F7.boolean.opBoolean","SPLIT",EDGE,{"disambiguationData":[TD([makeQuery(id+"F6.boolean.opBoolean","COPY",FACE,{"derivedFrom":makeQuery(id+"F6.opExtrude","CAP_FACE",FACE,{"disambiguationData":[OSD([sQuery(id+"F4.wireOp",EDGE,"E36"),subQ2,sQuery(id+"F4.wireOp",EDGE,"E38"),subQ0])],"isStart":true})})])],"derivedFrom":makeQuery(id+"F6.boolean.opBoolean","COPY",EDGE,{"derivedFrom":makeQuery(id+"F6.opExtrude","SWEPT_EDGE",EDGE,{"disambiguationData":[OSD([subQ2,subQ1,subQ0])]})})});}
            var Q22;
            Q22=makeQuery(id+"F5.opExtrude","CAP_EDGE",EDGE,{"disambiguationData":[OSD([sQuery(id+"F4.wireOp",EDGE,"E34")])],"isStart":true});
            var Q23;
            Q23=makeQuery(id+"F10.boolean.opBoolean","COPY",EDGE,{"derivedFrom":makeQuery(id+"F10.opExtrude","CAP_EDGE",EDGE,{"disambiguationData":[OSD([sQuery(id+"F9.wireOp",EDGE,"E52.MirrorCS")])],"isStart":true})});
            var Q24;
            Q24=makeQuery(id+"F10.boolean.opBoolean","COPY",EDGE,{"derivedFrom":makeQuery(id+"F10.opExtrude","CAP_EDGE",EDGE,{"disambiguationData":[OSD([sQuery(id+"F9.wireOp",EDGE,"E53.MirrorCS")])],"isStart":true})});
            var Q25;
            Q25=makeQuery(id+"F10.boolean.opBoolean","COPY",EDGE,{"derivedFrom":makeQuery(id+"F10.opExtrude","CAP_EDGE",EDGE,{"disambiguationData":[OSD([sQuery(id+"F9.wireOp",EDGE,"E54.MirrorCS")])],"isStart":true})});
            var Q26;
            Q26=makeQuery(id+"F10.boolean.opBoolean","COPY",EDGE,{"derivedFrom":makeQuery(id+"F10.opExtrude","SWEPT_EDGE",EDGE,{"disambiguationData":[OSD([sQuery(id+"F4.wireOp",EDGE,"E50"),sQuery(id+"F9.wireOp",EDGE,"E54.MirrorCS"),sQuery(id+"F9.wireOp",EDGE,"E55.MirrorCS")])]})});
            var Q27;
            Q27=makeQuery(id+"F10.boolean.opBoolean","COPY",EDGE,{"derivedFrom":makeQuery(id+"F10.opExtrude","SWEPT_EDGE",EDGE,{"disambiguationData":[OSD([sQuery(id+"F4.wireOp",EDGE,"E50"),sQuery(id+"F9.wireOp",EDGE,"E53.MirrorCS"),sQuery(id+"F9.wireOp",EDGE,"E55.MirrorCS")])]})});
            var Q28;
            Q28=makeQuery(id+"F10.boolean.opBoolean","COPY",EDGE,{"derivedFrom":makeQuery(id+"F10.opExtrude","CAP_EDGE",EDGE,{"disambiguationData":[OSD([sQuery(id+"F9.wireOp",EDGE,"E55.MirrorCS")])],"isStart":false})});
            var Q29;
            Q29=makeQuery(id+"F5.opExtrude","CAP_EDGE",EDGE,{"disambiguationData":[OSD([sQuery(id+"F4.wireOp",EDGE,"E30"),sQuery(id+"F4.wireOp",EDGE,"E32")])],"isStart":true});
            var Q30;
            Q30=makeQuery(id+"F5.opExtrude","CAP_EDGE",EDGE,{"disambiguationData":[OSD([sQuery(id+"F4.wireOp",EDGE,"E28")])],"isStart":true});
            var Q31;
            Q31=makeQuery(id+"F5.opExtrude","CAP_EDGE",EDGE,{"disambiguationData":[OSD([sQuery(id+"F4.wireOp",EDGE,"E28")])],"isStart":false});
            var Q32;
            Q32=makeQuery(id+"F7.boolean.opBoolean","COPY",EDGE,{"derivedFrom":makeQuery(id+"F7.opExtrude","CAP_EDGE",EDGE,{"disambiguationData":[OSD([sQuery(id+"F4.wireOp",EDGE,"E28")])],"isStart":false})});
            var Q33;
            Q33=makeQuery(id+"F7.boolean.opBoolean","COPY",EDGE,{"derivedFrom":makeQuery(id+"F7.opExtrude","CAP_EDGE",EDGE,{"disambiguationData":[OSD([sQuery(id+"F4.wireOp",EDGE,"E28")])],"isStart":true})});
            var Q34;
            Q34=makeQuery(id+"F7.boolean.opBoolean","COPY",EDGE,{"derivedFrom":makeQuery(id+"F7.opExtrude","CAP_EDGE",EDGE,{"disambiguationData":[OSD([sQuery(id+"F4.wireOp",EDGE,"E40")])],"isStart":true})});
            var Q35;
            Q35=makeQuery(id+"F7.boolean.opBoolean","COPY",EDGE,{"derivedFrom":makeQuery(id+"F7.opExtrude","CAP_EDGE",EDGE,{"disambiguationData":[OSD([sQuery(id+"F4.wireOp",EDGE,"E40")])],"isStart":false})});
            var Q36;
            Q36=makeQuery(id+"F5.opExtrude","CAP_EDGE",EDGE,{"disambiguationData":[OSD([sQuery(id+"F4.wireOp",EDGE,"E40")])],"isStart":false});
            var Q37;
            Q37=makeQuery(id+"F5.opExtrude","CAP_EDGE",EDGE,{"disambiguationData":[OSD([sQuery(id+"F4.wireOp",EDGE,"E40")])],"isStart":true});
            fillet(context, id + "F13", {"entities" : qUnion([Q0, Q1, Q2, Q3, Q4, Q5, Q6, Q7, Q8, Q9, Q10, Q11, Q12, Q13, Q14, Q15, Q16, Q17, Q18, Q19, Q20, Q21, Q22, Q23, Q24, Q25, Q26, Q27, Q28, Q29, Q30, Q31, Q32, Q33, Q34, Q35, Q36, Q37]), "radius" : 1 * mm, "tangentPropagation" : true, "allowEdgeOverflow" : false});
        }
        {
            var Q0;
            {var subQ0=sQuery(id+"F0.wireOp",EDGE,"E3");var subQ1=sQuery(id+"F0.wireOp",EDGE,"E0.bottom");Q0=makeQuery(id+"F2.boolean.opBoolean","MERGE",EDGE,{"derivedFrom":[makeQuery(id+"F1.opExtrude","SWEPT_EDGE",EDGE,{"disambiguationData":[OSD([subQ1,subQ0])]}),makeQuery(id+"F2.opExtrude","SWEPT_EDGE",EDGE,{"disambiguationData":[OSD([subQ1,subQ0])]})]});}
            var Q1;
            {var subQ0=sQuery(id+"F0.wireOp",EDGE,"E5");var subQ1=sQuery(id+"F0.wireOp",EDGE,"E0.bottom");Q1=makeQuery(id+"F2.boolean.opBoolean","MERGE",EDGE,{"derivedFrom":[makeQuery(id+"F1.opExtrude","SWEPT_EDGE",EDGE,{"disambiguationData":[OSD([subQ1,subQ0])]}),makeQuery(id+"F2.opExtrude","SWEPT_EDGE",EDGE,{"disambiguationData":[OSD([subQ1,subQ0])]})]});}
            var Q2;
            Q2=makeQuery(id+"F1.opExtrude","CAP_EDGE",EDGE,{"disambiguationData":[OSD([sQuery(id+"F0.wireOp",EDGE,"E3")])],"isStart":false});
            var Q3;
            Q3=makeQuery(id+"F1.opExtrude","CAP_EDGE",EDGE,{"disambiguationData":[OSD([sQuery(id+"F0.wireOp",EDGE,"E5")])],"isStart":false});
            var Q4;
            Q4=makeQuery(id+"F1.opExtrude","SWEPT_EDGE",EDGE,{"disambiguationData":[OSD([sQuery(id+"F0.wireOp",EDGE,"E0.top"),sQuery(id+"F0.wireOp",EDGE,"E3")])]});
            var Q5;
            Q5=makeQuery(id+"F1.opExtrude","SWEPT_EDGE",EDGE,{"disambiguationData":[OSD([sQuery(id+"F0.wireOp",EDGE,"E0.top"),sQuery(id+"F0.wireOp",EDGE,"E5")])]});
            var Q6;
            Q6=makeQuery(id+"F2.opExtrude","CAP_EDGE",EDGE,{"disambiguationData":[OSD([sQuery(id+"F0.wireOp",EDGE,"E0.top")])],"isStart":true});
            fillet(context, id + "F14", {"entities" : qUnion([Q0, Q1, Q2, Q3, Q4, Q5, Q6]), "radius" : 1 * mm, "tangentPropagation" : true, "allowEdgeOverflow" : false});
        }
        {
            var Q0;
            {var subQ0=sQuery(id+"F0.wireOp",EDGE,"E0.left");var subQ1=sQuery(id+"F0.wireOp",EDGE,"E0.bottom");Q0=makeQuery(id+"F2.boolean.opBoolean","MERGE",EDGE,{"derivedFrom":[makeQuery(id+"F1.opExtrude","SWEPT_EDGE",EDGE,{"disambiguationData":[OSD([subQ1,subQ0])]}),makeQuery(id+"F2.opExtrude","SWEPT_EDGE",EDGE,{"disambiguationData":[OSD([subQ1,subQ0])]})]});}
            var Q1;
            {var subQ0=sQuery(id+"F0.wireOp",EDGE,"E0.left");var subQ1=sQuery(id+"F0.wireOp",EDGE,"E0.top");Q1=makeQuery(id+"F2.boolean.opBoolean","MERGE",EDGE,{"derivedFrom":[makeQuery(id+"F1.opExtrude","SWEPT_EDGE",EDGE,{"disambiguationData":[OSD([subQ1,subQ0])]}),makeQuery(id+"F2.opExtrude","SWEPT_EDGE",EDGE,{"disambiguationData":[OSD([subQ1,subQ0])]})]});}
            var Q2;
            {var subQ0=sQuery(id+"F0.wireOp",EDGE,"E0.right");var subQ1=sQuery(id+"F0.wireOp",EDGE,"E0.bottom");Q2=makeQuery(id+"F2.boolean.opBoolean","MERGE",EDGE,{"derivedFrom":[makeQuery(id+"F1.opExtrude","SWEPT_EDGE",EDGE,{"disambiguationData":[OSD([subQ1,subQ0])]}),makeQuery(id+"F2.opExtrude","SWEPT_EDGE",EDGE,{"disambiguationData":[OSD([subQ1,subQ0])]})]});}
            var Q3;
            {var subQ0=sQuery(id+"F0.wireOp",EDGE,"E0.right");var subQ1=sQuery(id+"F0.wireOp",EDGE,"E0.top");Q3=makeQuery(id+"F2.boolean.opBoolean","MERGE",EDGE,{"derivedFrom":[makeQuery(id+"F1.opExtrude","SWEPT_EDGE",EDGE,{"disambiguationData":[OSD([subQ1,subQ0])]}),makeQuery(id+"F2.opExtrude","SWEPT_EDGE",EDGE,{"disambiguationData":[OSD([subQ1,subQ0])]})]});}
            fillet(context, id + "F15", {"entities" : qUnion([Q0, Q1, Q2, Q3]), "radius" : 7 * mm, "tangentPropagation" : true, "allowEdgeOverflow" : false});
        }
        {
            var Q0;
            {var subQ7=sQuery(id+"F0.wireOp",EDGE,"E8");Q0=makeQuery(id+"F0.imprint","IMPRINT",FACE,{"disambiguationData":[TD([[makeQuery(id+"F0.imprint","IMPRINT",EDGE,{"derivedFrom":subQ7}),1.0]])]});}
            var Q1;
            {var subQ0=sQuery(id+"F0.wireOp",EDGE,"E21");Q1=makeQuery(id+"F0.imprint","IMPRINT",FACE,{"disambiguationData":[TD([[makeQuery(id+"F0.imprint","IMPRINT",EDGE,{"derivedFrom":subQ0}),-1.0]])]});}
            var Q2;
            {var subQ2=sQuery(id+"F0.wireOp",EDGE,"E19");Q2=makeQuery(id+"F0.imprint","IMPRINT",FACE,{"disambiguationData":[TD([[makeQuery(id+"F0.imprint","IMPRINT",EDGE,{"derivedFrom":subQ2}),-1.0]])]});}
            extrude(context, id + "F16", {"entities" : qUnion([Q0, Q1, Q2]), "depth" : 30 * mm});
        }
        {
            var Q0;
            Q0=makeQuery(id+"F16.opExtrude","SWEPT_EDGE",EDGE,{"disambiguationData":[OSD([sQuery(id+"F0.wireOp",EDGE,"E8"),sQuery(id+"F0.wireOp",EDGE,"E9")])]});
            var Q1;
            Q1=makeQuery(id+"F16.opExtrude","SWEPT_EDGE",EDGE,{"disambiguationData":[OSD([sQuery(id+"F0.wireOp",EDGE,"E10"),sQuery(id+"F0.wireOp",EDGE,"E11")])]});
            var Q2;
            Q2=makeQuery(id+"F16.opExtrude","SWEPT_EDGE",EDGE,{"disambiguationData":[OSD([sQuery(id+"F0.wireOp",EDGE,"E7"),sQuery(id+"F0.wireOp",EDGE,"E8")])]});
            fillet(context, id + "F17", {"entities" : qUnion([Q0, Q1, Q2]), "radius" : 3 * mm, "tangentPropagation" : true, "allowEdgeOverflow" : false});
        }
        {
            var Q0;
            Q0=makeQuery(id+"F16.opExtrude","SWEPT_EDGE",EDGE,{"disambiguationData":[OSD([sQuery(id+"F0.wireOp",EDGE,"E9"),sQuery(id+"F0.wireOp",EDGE,"E10")])]});
            fillet(context, id + "F18", {"entities" : qUnion([Q0]), "radius" : 1 * mm, "tangentPropagation" : true, "allowEdgeOverflow" : false});
        }
        {
            var Q0;
            {var subQ0=sQuery(id+"F0.wireOp",EDGE,"E11");var subQ1=sQuery(id+"F0.wireOp",EDGE,"E10");Q0=makeQuery(id+"F17.opFillet","BLEND_EDGE",EDGE,{"blendedFrom":[makeQuery(id+"F16.opExtrude","SWEPT_EDGE",EDGE,{"disambiguationData":[OSD([subQ1,subQ0])]}),makeQuery(id+"F16.opExtrude","CAP_FACE",FACE,{"disambiguationData":[OSD([sQuery(id+"F0.wireOp",EDGE,"E7"),sQuery(id+"F0.wireOp",EDGE,"E8"),sQuery(id+"F0.wireOp",EDGE,"E9"),subQ1,subQ0,sQuery(id+"F0.wireOp",EDGE,"E12"),sQuery(id+"F0.wireOp",EDGE,"E13"),sQuery(id+"F0.wireOp",EDGE,"E14"),sQuery(id+"F0.wireOp",EDGE,"E15"),sQuery(id+"F0.wireOp",EDGE,"E16"),sQuery(id+"F0.wireOp",EDGE,"E17"),sQuery(id+"F0.wireOp",EDGE,"E18"),sQuery(id+"F0.wireOp",EDGE,"E19"),sQuery(id+"F0.wireOp",EDGE,"E20"),sQuery(id+"F0.wireOp",EDGE,"E21"),sQuery(id+"F0.wireOp",EDGE,"E22")])],"isStart":true})],"blendedInto":[makeQuery(id+"F16.opExtrude","CAP_FACE",FACE,{"disambiguationData":[OSD([sQuery(id+"F0.wireOp",EDGE,"E7"),sQuery(id+"F0.wireOp",EDGE,"E8"),sQuery(id+"F0.wireOp",EDGE,"E9"),subQ1,subQ0,sQuery(id+"F0.wireOp",EDGE,"E12"),sQuery(id+"F0.wireOp",EDGE,"E13"),sQuery(id+"F0.wireOp",EDGE,"E14"),sQuery(id+"F0.wireOp",EDGE,"E15"),sQuery(id+"F0.wireOp",EDGE,"E16"),sQuery(id+"F0.wireOp",EDGE,"E17"),sQuery(id+"F0.wireOp",EDGE,"E18"),sQuery(id+"F0.wireOp",EDGE,"E19"),sQuery(id+"F0.wireOp",EDGE,"E20"),sQuery(id+"F0.wireOp",EDGE,"E21"),sQuery(id+"F0.wireOp",EDGE,"E22")])],"isStart":true})]});}
            var Q1;
            Q1=makeQuery(id+"F16.opExtrude","CAP_EDGE",EDGE,{"disambiguationData":[OSD([sQuery(id+"F0.wireOp",EDGE,"E12")])],"isStart":true});
            var Q2;
            Q2=makeQuery(id+"F16.opExtrude","CAP_EDGE",EDGE,{"disambiguationData":[OSD([sQuery(id+"F0.wireOp",EDGE,"E13")])],"isStart":true});
            var Q3;
            Q3=makeQuery(id+"F16.opExtrude","CAP_EDGE",EDGE,{"disambiguationData":[OSD([sQuery(id+"F0.wireOp",EDGE,"E22")])],"isStart":true});
            var Q4;
            Q4=makeQuery(id+"F16.opExtrude","CAP_EDGE",EDGE,{"disambiguationData":[OSD([sQuery(id+"F0.wireOp",EDGE,"E19")])],"isStart":true});
            var Q5;
            Q5=makeQuery(id+"F16.opExtrude","CAP_EDGE",EDGE,{"disambiguationData":[OSD([sQuery(id+"F0.wireOp",EDGE,"E12")])],"isStart":false});
            var Q6;
            {var subQ0=sQuery(id+"F0.wireOp",EDGE,"E11");var subQ1=sQuery(id+"F0.wireOp",EDGE,"E10");Q6=makeQuery(id+"F17.opFillet","BLEND_EDGE",EDGE,{"blendedFrom":[makeQuery(id+"F16.opExtrude","SWEPT_EDGE",EDGE,{"disambiguationData":[OSD([subQ1,subQ0])]}),makeQuery(id+"F16.opExtrude","CAP_FACE",FACE,{"disambiguationData":[OSD([sQuery(id+"F0.wireOp",EDGE,"E7"),sQuery(id+"F0.wireOp",EDGE,"E8"),sQuery(id+"F0.wireOp",EDGE,"E9"),subQ1,subQ0,sQuery(id+"F0.wireOp",EDGE,"E12"),sQuery(id+"F0.wireOp",EDGE,"E13"),sQuery(id+"F0.wireOp",EDGE,"E14"),sQuery(id+"F0.wireOp",EDGE,"E15"),sQuery(id+"F0.wireOp",EDGE,"E16"),sQuery(id+"F0.wireOp",EDGE,"E17"),sQuery(id+"F0.wireOp",EDGE,"E18"),sQuery(id+"F0.wireOp",EDGE,"E19"),sQuery(id+"F0.wireOp",EDGE,"E20"),sQuery(id+"F0.wireOp",EDGE,"E21"),sQuery(id+"F0.wireOp",EDGE,"E22")])],"isStart":false})],"blendedInto":[makeQuery(id+"F16.opExtrude","CAP_FACE",FACE,{"disambiguationData":[OSD([sQuery(id+"F0.wireOp",EDGE,"E7"),sQuery(id+"F0.wireOp",EDGE,"E8"),sQuery(id+"F0.wireOp",EDGE,"E9"),subQ1,subQ0,sQuery(id+"F0.wireOp",EDGE,"E12"),sQuery(id+"F0.wireOp",EDGE,"E13"),sQuery(id+"F0.wireOp",EDGE,"E14"),sQuery(id+"F0.wireOp",EDGE,"E15"),sQuery(id+"F0.wireOp",EDGE,"E16"),sQuery(id+"F0.wireOp",EDGE,"E17"),sQuery(id+"F0.wireOp",EDGE,"E18"),sQuery(id+"F0.wireOp",EDGE,"E19"),sQuery(id+"F0.wireOp",EDGE,"E20"),sQuery(id+"F0.wireOp",EDGE,"E21"),sQuery(id+"F0.wireOp",EDGE,"E22")])],"isStart":false})]});}
            var Q7;
            Q7=makeQuery(id+"F16.opExtrude","CAP_EDGE",EDGE,{"disambiguationData":[OSD([sQuery(id+"F0.wireOp",EDGE,"E13")])],"isStart":false});
            var Q8;
            Q8=makeQuery(id+"F16.opExtrude","CAP_EDGE",EDGE,{"disambiguationData":[OSD([sQuery(id+"F0.wireOp",EDGE,"E22")])],"isStart":false});
            var Q9;
            Q9=makeQuery(id+"F16.opExtrude","CAP_EDGE",EDGE,{"disambiguationData":[OSD([sQuery(id+"F0.wireOp",EDGE,"E19")])],"isStart":false});
            fillet(context, id + "F19", {"entities" : qUnion([Q0, Q1, Q2, Q3, Q4, Q5, Q6, Q7, Q8, Q9]), "radius" : 1 * mm, "tangentPropagation" : true, "allowEdgeOverflow" : false});
        }
        {
            var Q0;
            Q0=makeQuery(id+"F16.opExtrude","SWEPT_BODY",BODY,{"disambiguationData":[OSD([sQuery(id+"F0.wireOp",EDGE,"E7"),sQuery(id+"F0.wireOp",EDGE,"E8"),sQuery(id+"F0.wireOp",EDGE,"E9"),sQuery(id+"F0.wireOp",EDGE,"E10"),sQuery(id+"F0.wireOp",EDGE,"E11"),sQuery(id+"F0.wireOp",EDGE,"E12"),sQuery(id+"F0.wireOp",EDGE,"E13"),sQuery(id+"F0.wireOp",EDGE,"E14"),sQuery(id+"F0.wireOp",EDGE,"E15"),sQuery(id+"F0.wireOp",EDGE,"E16"),sQuery(id+"F0.wireOp",EDGE,"E17"),sQuery(id+"F0.wireOp",EDGE,"E18"),sQuery(id+"F0.wireOp",EDGE,"E19"),sQuery(id+"F0.wireOp",EDGE,"E20"),sQuery(id+"F0.wireOp",EDGE,"E21"),sQuery(id+"F0.wireOp",EDGE,"E22")])]});
            transform(context, id + "F20", {"entities" : qUnion([Q0]), "transformType" : TransformType.TRANSLATION_3D, "dx" : -2 * mm, "dy" : 0 * mm, "dz" : 0 * mm, "makeCopy" : false});
        }
        {
            var Q0;
            Q0=makeQuery(id+"F16.opExtrude","SWEPT_BODY",BODY,{"disambiguationData":[OSD([sQuery(id+"F0.wireOp",EDGE,"E7"),sQuery(id+"F0.wireOp",EDGE,"E8"),sQuery(id+"F0.wireOp",EDGE,"E9"),sQuery(id+"F0.wireOp",EDGE,"E10"),sQuery(id+"F0.wireOp",EDGE,"E11"),sQuery(id+"F0.wireOp",EDGE,"E12"),sQuery(id+"F0.wireOp",EDGE,"E13"),sQuery(id+"F0.wireOp",EDGE,"E14"),sQuery(id+"F0.wireOp",EDGE,"E15"),sQuery(id+"F0.wireOp",EDGE,"E16"),sQuery(id+"F0.wireOp",EDGE,"E17"),sQuery(id+"F0.wireOp",EDGE,"E18"),sQuery(id+"F0.wireOp",EDGE,"E19"),sQuery(id+"F0.wireOp",EDGE,"E20"),sQuery(id+"F0.wireOp",EDGE,"E21"),sQuery(id+"F0.wireOp",EDGE,"E22")])]});
            var Q1;
            Q1=qCreatedBy(makeId("Right.planeOp"),FACE);
            mirror(context, id + "F21", {"entities" : qUnion([Q0]), "mirrorPlane" : qUnion([Q1])});
        }
    });
